# Revit family: Painel Supervisor Endereçável PRM ILUMAC
name_source: partatom
category: Dispositivos de alarme de incêndio
units: mm (PartAtom-declared; Revit-internal decimal feet)

## family parameters
Com base no plano de trabalho = Não
Compartilhado = Não
Corte com vazios quando carregada = Não
Cota do conector redondo = Utilizar diâmetro
Manter orientação da anotação = Não
Número OmniClass = 23.75.00.00
Ponto de cálculo do ambiente = Não
Sempre na vertical = Sim
Tipo de parte = Normal
Título OmniClass = Climate Control (HVAC)

## types (2) — shared parameters
Alimentação principal da rede elétrica = 100 a 240VCA – 50/60Hz
Alimentação secundária = 24VCC (2 baterias seladas de 12VCC - 2,2Ah)
Bornes para conexão dos condutores = KRE p/ 1,5mm² à 2,5mm²
Consumo de energia da rede elétrica = 62 Watts
Corrente de recarga das baterias = 400mA @ 27,6VCC nominal 25ºC
Correntes de consumo = 115mA @ 24VCC em supervisão
180mA @ 24VCC em alarme
Dimensões (AxLxP) = 255x230x100mm
Fabricante = ILUMAC
Fixação = Sobrepor, com 3 parafusos (acompanha)
Grau de proteção = IP20 (uso interno)
Material da caixa = Plástico ABS preto
Normas técnicas aplicáveis = ABNT NBR 17.240:2010 | ABNT NBR ISO 7240-4
Painel frontal (IHM) = 8 LEDs / 4 teclas / LCD 2x32 com backlight
Peso = 1,8Kg (sem baterias)
3,0Kg (com 2 baterias de 12VCC - 2,2Ah)
Proteção na entrada da rede elétrica = Fusível de vidro 20AG - 2A (fusão rápida)
Proteção na entrada das baterias = Fusível rearmável - PTC 3A @ 24VCC (25ºC)
Relógio = RTC com data e hora
Saída da fonte de alimentação = 1,0A @ 28VCC - 25ºC
Saída para sirenes convencionais = 1 saída de 2A @ 24VCC
Saída rele auxiliar = 1 saída contato seco / 1A até 30V (carga resistiva)
Temperatura de operação = 0 a 40ºC
Tensão de ativação dos laços = < 06V
Tensão nominal e de operação = 24VCC / 22 à 28VCC
Topologia = Classe A ou Classe B (3 fios)
Umidade relativa = Máximo 95%, sem condensação
zero-valued in all types: Elevação padrão

## per-type parameters (varying)
| type | Código do produto | Descrição | Entrada para programação via PC | Modelo | Protocolo de comunicação |
| PRM-E PRETO | 002216 | Painel Repetidor Endereçável PRM-E preto | 1 entrada mini-USB para conexão com o PUC-E | PRM-E | ALF-500 (Exclusivo da ILUMAC) |
| PRM-D | 0040010 | Painel Repetidor Endereçável Sirius PRM-D | 1 entrada mini-USB para conexão com o PUC-D | PRM-D | ALF-1000-2 (Exclusivo da ILUMAC) |
